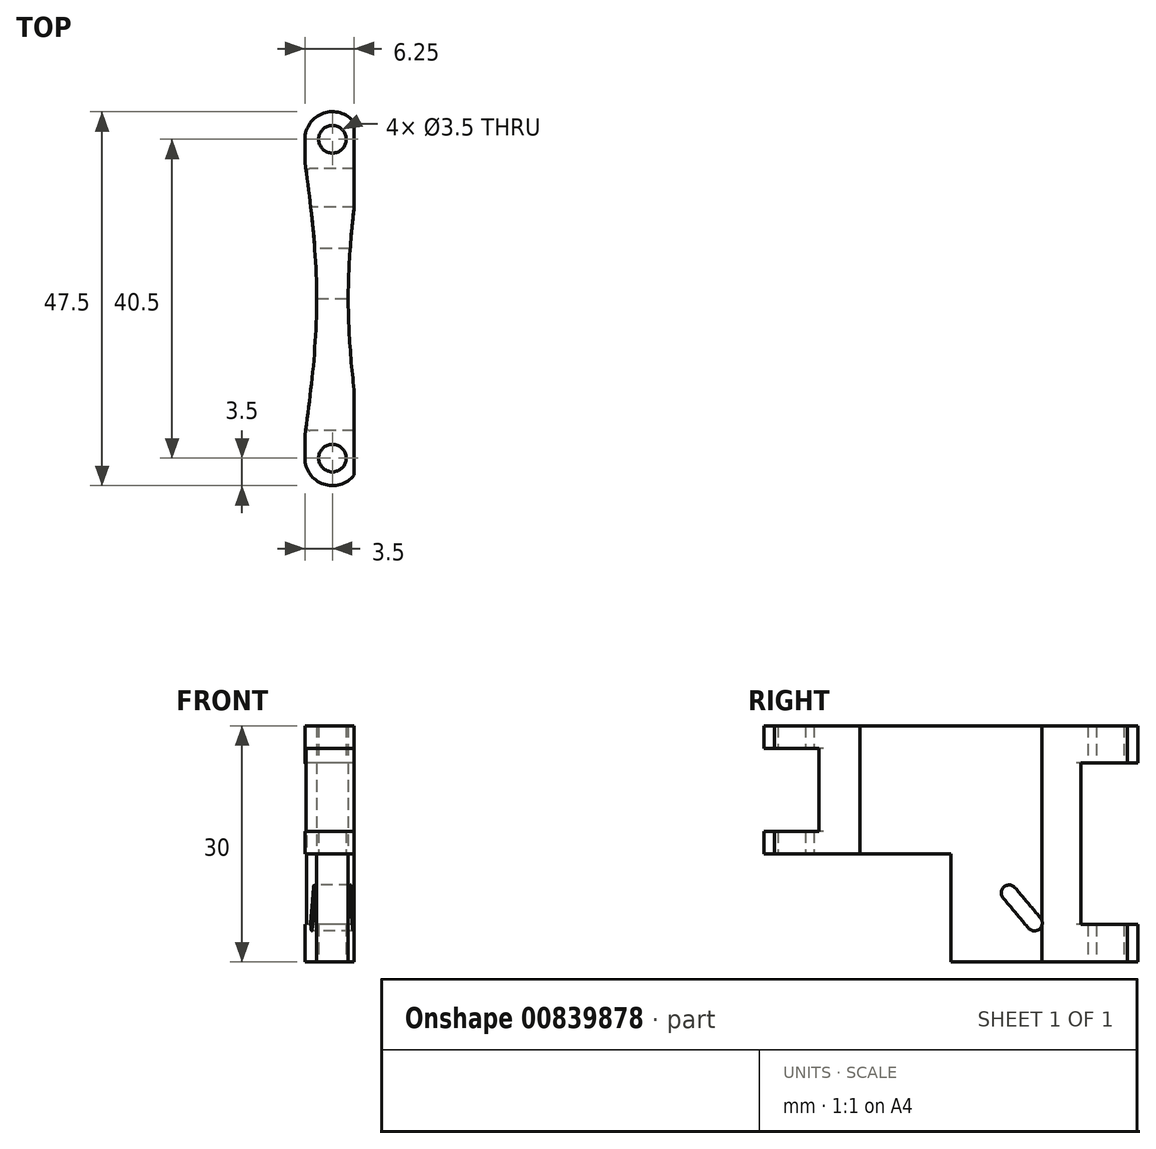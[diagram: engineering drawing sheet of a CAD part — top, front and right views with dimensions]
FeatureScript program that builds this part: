
annotation { "Feature Type Name" : "Feature", "Feature Type Description" : "" }
export const myFeature = defineFeature(function(context is Context, id is Id, definition is map)
    precondition{}
    {
        {
            var Q0;
            Q0=qCreatedBy(makeId("Top.planeOp"),FACE);
            var sketch = newSketch(context, id + "F0", { "sketchPlane" : qUnion([Q0])});
            skCircle(sketch, "E0", {"center": v(0, 0) * mm, "radius": 1.75 * mm});
            skCircle(sketch, "E1", {"center": v(0, 0) * mm, "radius": 3.5 * mm});
            skCircle(sketch, "E2", {"center": v(0, 40.5) * mm, "radius": 3.5 * mm});
            skCircle(sketch, "E3", {"center": v(0, 40.5) * mm, "radius": 1.75 * mm});
            skLineSegment(sketch, "E4", {"start": v(-3.5, 40.5) * mm, "end": v(-3.5, 0) * mm});
            skLineSegment(sketch, "E5", {"start": v(3.5, 40.5) * mm, "end": v(3.5, 0) * mm});
            skLineSegment(sketch, "E6", {"start": v(-2, 37.63) * mm, "end": v(-2, 2.87) * mm, "construction": true});
            skLineSegment(sketch, "E7", {"start": v(-2, 20.25) * mm, "end": v(-3.5, 20.25) * mm, "construction": true});
            skFitSpline(sketch, "E8", {"points": [v(-3.5, 37.63) * mm, v(-2, 20.25) * mm, v(-3.5, 2.87) * mm], "startDerivative": vector(4.5, -32.27) * mm, "endDerivative": vector(-4.5, -32.27) * mm});
            skLineSegment(sketch, "E9", {"start": v(-2.75, 20.25) * mm, "end": v(-2.75, 38.33) * mm, "construction": true});
            skLineSegment(sketch, "E10", {"start": v(-2.75, 20.25) * mm, "end": v(-2.75, 2.17) * mm, "construction": true});
            skFitSpline(sketch, "E11.MirrorCS", {"points": [v(3.5, 37.63) * mm, v(2, 20.25) * mm, v(3.5, 2.87) * mm], "startDerivative": vector(-4.5, -32.27) * mm, "endDerivative": vector(4.5, -32.27) * mm});
            skLineSegment(sketch, "E12", {"start": v(-3.5, 20.25) * mm, "end": v(3.5, 20.25) * mm});
            skSolve(sketch);
        }
        {
            var Q0;
            {var subQ0=sQuery(id+"F0.wireOp",EDGE,"E8");var subQ1=sQuery(id+"F0.wireOp",EDGE,"E2");var subQ2=makeQuery(id+"F0.imprint","INTERSECT",VERTEX,{"disambiguationData":[OD(1.0)],"derivedFrom":[subQ1,subQ0]});Q0=makeQuery(id+"F0.imprint","IMPRINT",FACE,{"disambiguationData":[TD([[makeQuery(id+"F0.imprint","IMPRINT",EDGE,{"disambiguationData":[TD([[subQ2,-1.0]])],"derivedFrom":subQ1}),-1.0]])]});}
            var Q1;
            {var subQ0=sQuery(id+"F0.wireOp",EDGE,"E11.MirrorCS");var subQ1=sQuery(id+"F0.wireOp",EDGE,"E1");var subQ2=makeQuery(id+"F0.imprint","INTERSECT",VERTEX,{"disambiguationData":[OD(1.0)],"derivedFrom":[subQ1,subQ0]});Q1=makeQuery(id+"F0.imprint","IMPRINT",FACE,{"disambiguationData":[TD([[makeQuery(id+"F0.imprint","IMPRINT",EDGE,{"disambiguationData":[TD([[subQ2,-1.0]])],"derivedFrom":subQ1}),-1.0]])]});}
            var Q2;
            Q2=makeQuery(id+"F0.imprint","IMPRINT",FACE,{"disambiguationData":[TD([[makeQuery(id+"F0.imprint","IMPRINT",EDGE,{"derivedFrom":sQuery(id+"F0.wireOp",EDGE,"E0")}),-1.0]])]});
            var Q3;
            Q3=makeQuery(id+"F0.imprint","IMPRINT",FACE,{"disambiguationData":[TD([[makeQuery(id+"F0.imprint","IMPRINT",EDGE,{"derivedFrom":sQuery(id+"F0.wireOp",EDGE,"E3")}),-1.0]])]});
            var Q4;
            {var subQ1=sQuery(id+"F0.wireOp",EDGE,"E2");var subQ5=sQuery(id+"F0.wireOp",EDGE,"E4");var subQ6=makeQuery(id+"F0.imprint","INTERSECT",VERTEX,{"derivedFrom":[subQ1,subQ5]});Q4=makeQuery(id+"F0.imprint","IMPRINT",FACE,{"disambiguationData":[TD([[makeQuery(id+"F0.imprint","IMPRINT",EDGE,{"disambiguationData":[TD([[subQ6,-1.0]])],"derivedFrom":subQ1}),-1.0]])]});}
            var Q5;
            {var subQ1=sQuery(id+"F0.wireOp",EDGE,"E4");var subQ6=sQuery(id+"F0.wireOp",EDGE,"E1");var subQ10=makeQuery(id+"F0.imprint","INTERSECT",VERTEX,{"derivedFrom":[subQ6,subQ1]});Q5=makeQuery(id+"F0.imprint","IMPRINT",FACE,{"disambiguationData":[TD([[makeQuery(id+"F0.imprint","IMPRINT",EDGE,{"disambiguationData":[TD([[subQ10,1.0]])],"derivedFrom":subQ6}),-1.0]])]});}
            extrude(context, id + "F1", {"entities" : qUnion([Q0, Q1, Q2, Q3, Q4, Q5]), "depth" : (30 - 13.7) * mm, "offsetDistance" : 25 * mm});
        }
        {
            var Q0;
            {var subQ0=sQuery(id+"F0.wireOp",EDGE,"E4");Q0=makeQuery(id+"F1.opExtrude","SWEPT_FACE",FACE,{"disambiguationData":[OSD([subQ0]),TDD([makeQuery(id+"F0.imprint","IMPRINT",EDGE,{"disambiguationData":[TD([[makeQuery(id+"F0.imprint","INTERSECT",VERTEX,{"derivedFrom":[sQuery(id+"F0.wireOp",EDGE,"E1"),subQ0]}),1.0]])],"derivedFrom":subQ0})])]});}
            var sketch = newSketch(context, id + "F2", { "sketchPlane" : qUnion([Q0])});
            skLineSegment(sketch, "E13.bottom", {"start": v(3.5, 2.9) * mm, "end": v(-3.5, 2.9) * mm});
            skLineSegment(sketch, "E13.top", {"start": v(3.5, 13.4) * mm, "end": v(-3.5, 13.4) * mm});
            skLineSegment(sketch, "E13.left", {"start": v(3.5, 2.9) * mm, "end": v(3.5, 13.4) * mm});
            skLineSegment(sketch, "E13.right", {"start": v(-3.5, 2.9) * mm, "end": v(-3.5, 13.4) * mm});
            skPoint(sketch, "E13.middle", {"position": v(0, 8.15) * mm});
            skSolve(sketch);
        }
        {
            var Q0;
            {var subQ0=sQuery(id+"F2.wireOp",EDGE,"E13.right");Q0=makeQuery(id+"F2.imprint","IMPRINT",FACE,{"disambiguationData":[TD([[makeQuery(id+"F2.imprint","IMPRINT",EDGE,{"derivedFrom":subQ0}),-1.0]])]});}
            var Q1;
            {var subQ0=sQuery(id+"F2.wireOp",EDGE,"E13.bottom");var subQ1=sQuery(id+"F0.wireOp",EDGE,"E4");var subQ2=makeQuery(id+"F1.opExtrude","SWEPT_EDGE",EDGE,{"disambiguationData":[OSD([sQuery(id+"F0.wireOp",EDGE,"E1"),subQ1])]});var subQ3=makeQuery(id+"F2.imprint","INTERSECT",VERTEX,{"derivedFrom":[subQ2,subQ0]});Q1=makeQuery(id+"F2.imprint","IMPRINT",FACE,{"disambiguationData":[TD([[makeQuery(id+"F2.imprint","IMPRINT",EDGE,{"disambiguationData":[TD([[subQ3,-1.0]])],"derivedFrom":subQ0}),-1.0]])]});}
            var Q2;
            {var subQ0=sQuery(id+"F2.wireOp",EDGE,"E13.left");Q2=makeQuery(id+"F2.imprint","IMPRINT",FACE,{"disambiguationData":[TD([[makeQuery(id+"F2.imprint","IMPRINT",EDGE,{"derivedFrom":subQ0}),1.0]])]});}
            extrude(context, id + "F3", {"entities" : qUnion([Q0, Q1, Q2]), "operationType" : NewBodyOperationType.REMOVE, "oppositeDirection" : true, "depth" : 25 * mm, "offsetDistance" : 25 * mm});
        }
        {
            var Q0;
            Q0=makeQuery(id+"F0.imprint","IMPRINT",FACE,{"disambiguationData":[TD([[makeQuery(id+"F0.imprint","IMPRINT",EDGE,{"derivedFrom":sQuery(id+"F0.wireOp",EDGE,"E3")}),-1.0]])]});
            var Q1;
            {var subQ1=sQuery(id+"F0.wireOp",EDGE,"E2");var subQ5=sQuery(id+"F0.wireOp",EDGE,"E4");var subQ6=makeQuery(id+"F0.imprint","INTERSECT",VERTEX,{"derivedFrom":[subQ1,subQ5]});Q1=makeQuery(id+"F0.imprint","IMPRINT",FACE,{"disambiguationData":[TD([[makeQuery(id+"F0.imprint","IMPRINT",EDGE,{"disambiguationData":[TD([[subQ6,-1.0]])],"derivedFrom":subQ1}),-1.0]])]});}
            extrude(context, id + "F4", {"entities" : qUnion([Q0, Q1]), "operationType" : NewBodyOperationType.ADD, "depth" : -13.7 * mm, "offsetDistance" : 25 * mm});
        }
        {
            var Q0;
            {var subQ0=sQuery(id+"F0.wireOp",EDGE,"E4");Q0=makeQuery(id+"F4.boolean.opBoolean","MERGE",FACE,{"derivedFrom":[makeQuery(id+"F1.opExtrude","SWEPT_FACE",FACE,{"disambiguationData":[OSD([subQ0]),TDD([makeQuery(id+"F0.imprint","IMPRINT",EDGE,{"disambiguationData":[TD([[makeQuery(id+"F0.imprint","INTERSECT",VERTEX,{"derivedFrom":[sQuery(id+"F0.wireOp",EDGE,"E2"),subQ0]}),-1.0]])],"derivedFrom":subQ0})])]}),makeQuery(id+"F4.opExtrude","SWEPT_FACE",FACE,{"disambiguationData":[OSD([subQ0])]})]});}
            var sketch = newSketch(context, id + "F5", { "sketchPlane" : qUnion([Q0])});
            skLineSegment(sketch, "E14.bottom", {"start": v(-36.75, 11.55) * mm, "end": v(-44.25, 11.55) * mm});
            skLineSegment(sketch, "E14.top", {"start": v(-36.75, -8.95) * mm, "end": v(-44.25, -8.95) * mm});
            skLineSegment(sketch, "E14.left", {"start": v(-36.75, 11.55) * mm, "end": v(-36.75, -8.95) * mm});
            skLineSegment(sketch, "E14.right", {"start": v(-44.25, 11.55) * mm, "end": v(-44.25, -8.95) * mm});
            skPoint(sketch, "E14.middle", {"position": v(-40.5, 1.3) * mm});
            skLineSegment(sketch, "E15", {"start": v(-21.75, 0) * mm, "end": v(-36.75, 0) * mm, "construction": true});
            skLineSegment(sketch, "E16", {"start": v(-36.75, 0) * mm, "end": v(-36.75, -13.7) * mm, "construction": true});
            skLineSegment(sketch, "E17", {"start": v(-36.75, -13.7) * mm, "end": v(-21.75, -13.7) * mm, "construction": true});
            skLineSegment(sketch, "E18", {"start": v(-21.75, -13.7) * mm, "end": v(-21.75, 0) * mm, "construction": true});
            skLineSegment(sketch, "E19", {"start": v(-21.75, 0) * mm, "end": v(-21.75, -6.85) * mm, "construction": true});
            skLineSegment(sketch, "E20", {"start": v(-21.75, -13.7) * mm, "end": v(-21.75, -6.85) * mm, "construction": true});
            skCircle(sketch, "E21", {"center": v(-30.86, -8.77) * mm, "radius": 1 * mm});
            skCircle(sketch, "E22", {"center": v(-27.64, -4.93) * mm, "radius": 1 * mm});
            skLineSegment(sketch, "E23", {"start": v(-28.4, -4.3) * mm, "end": v(-31.62, -8.12) * mm});
            skLineSegment(sketch, "E24", {"start": v(-26.88, -5.58) * mm, "end": v(-30.1, -9.4) * mm});
            skLineSegment(sketch, "E25", {"start": v(-21.75, -6.85) * mm, "end": v(-36.75, -6.85) * mm, "construction": true});
            skLineSegment(sketch, "E26", {"start": v(-29.25, -6.85) * mm, "end": v(-27.64, -4.93) * mm, "construction": true});
            skLineSegment(sketch, "E27", {"start": v(-29.25, -6.85) * mm, "end": v(-30.86, -8.77) * mm, "construction": true});
            skLineSegment(sketch, "E28", {"start": v(-29.25, -6.85) * mm, "end": v(-21.75, -6.85) * mm, "construction": true});
            skSolve(sketch);
        }
        {
            var Q0;
            {var subQ0=sQuery(id+"F5.wireOp",EDGE,"E14.right");Q0=makeQuery(id+"F5.imprint","IMPRINT",FACE,{"disambiguationData":[TD([[makeQuery(id+"F5.imprint","IMPRINT",EDGE,{"derivedFrom":subQ0}),1.0]])]});}
            var Q1;
            {var subQ0=sQuery(id+"F5.wireOp",EDGE,"E14.bottom");var subQ2=sQuery(id+"F0.wireOp",EDGE,"E4");var subQ5=sQuery(id+"F0.wireOp",EDGE,"E2");var subQ6=makeQuery(id+"F4.boolean.opBoolean","MERGE",EDGE,{"derivedFrom":[makeQuery(id+"F1.opExtrude","SWEPT_EDGE",EDGE,{"disambiguationData":[OSD([subQ5,subQ2])]}),makeQuery(id+"F4.opExtrude","SWEPT_EDGE",EDGE,{"disambiguationData":[OSD([subQ5,subQ2])]})]});var subQ7=makeQuery(id+"F5.imprint","INTERSECT",VERTEX,{"derivedFrom":[subQ6,subQ0]});Q1=makeQuery(id+"F5.imprint","IMPRINT",FACE,{"disambiguationData":[TD([[makeQuery(id+"F5.imprint","IMPRINT",EDGE,{"disambiguationData":[TD([[subQ7,1.0]])],"derivedFrom":subQ0}),1.0]])]});}
            var Q2;
            {var subQ0=sQuery(id+"F5.wireOp",EDGE,"E14.left");Q2=makeQuery(id+"F5.imprint","IMPRINT",FACE,{"disambiguationData":[TD([[makeQuery(id+"F5.imprint","IMPRINT",EDGE,{"derivedFrom":subQ0}),-1.0]])]});}
            var Q3;
            {var subQ0=sQuery(id+"F5.wireOp",EDGE,"E21");var subQ1=makeQuery(id+"F5.imprint","INTERSECT",VERTEX,{"derivedFrom":[subQ0,sQuery(id+"F5.wireOp",EDGE,"E23")]});Q3=makeQuery(id+"F5.imprint","IMPRINT",FACE,{"disambiguationData":[TD([[makeQuery(id+"F5.imprint","IMPRINT",EDGE,{"disambiguationData":[TD([[subQ1,-1.0]])],"derivedFrom":subQ0}),1.0]])]});}
            var Q4;
            {var subQ0=sQuery(id+"F5.wireOp",EDGE,"E23");Q4=makeQuery(id+"F5.imprint","IMPRINT",FACE,{"disambiguationData":[TD([[makeQuery(id+"F5.imprint","IMPRINT",EDGE,{"derivedFrom":subQ0}),1.0]])]});}
            var Q5;
            {var subQ0=sQuery(id+"F5.wireOp",EDGE,"E22");var subQ1=makeQuery(id+"F5.imprint","INTERSECT",VERTEX,{"derivedFrom":[subQ0,sQuery(id+"F5.wireOp",EDGE,"E23")]});Q5=makeQuery(id+"F5.imprint","IMPRINT",FACE,{"disambiguationData":[TD([[makeQuery(id+"F5.imprint","IMPRINT",EDGE,{"disambiguationData":[TD([[subQ1,-1.0]])],"derivedFrom":subQ0}),1.0]])]});}
            extrude(context, id + "F6", {"entities" : qUnion([Q0, Q1, Q2, Q3, Q4, Q5]), "operationType" : NewBodyOperationType.REMOVE, "oppositeDirection" : true, "depth" : 25 * mm, "offsetDistance" : 25 * mm});
        }
        {
            var Q0;
            Q0=makeQuery(id+"F3.boolean.opBoolean","INTERSECT",EDGE,{"derivedFrom":[makeQuery(id+"F1.opExtrude","SWEPT_FACE",FACE,{"disambiguationData":[OSD([sQuery(id+"F0.wireOp",EDGE,"E8")])]}),makeQuery(id+"F3.opExtrude","SWEPT_FACE",FACE,{"disambiguationData":[OSD([sQuery(id+"F2.wireOp",EDGE,"E13.right")])]})]});
            var Q1;
            Q1=makeQuery(id+"F3.boolean.opBoolean","INTERSECT",EDGE,{"derivedFrom":[makeQuery(id+"F1.opExtrude","SWEPT_FACE",FACE,{"disambiguationData":[OSD([sQuery(id+"F0.wireOp",EDGE,"E11.MirrorCS")])]}),makeQuery(id+"F3.opExtrude","SWEPT_FACE",FACE,{"disambiguationData":[OSD([sQuery(id+"F2.wireOp",EDGE,"E13.right")])]})]});
            var Q2;
            {var subQ0=sQuery(id+"F0.wireOp",EDGE,"E11.MirrorCS");Q2=makeQuery(id+"F6.boolean.opBoolean","INTERSECT",EDGE,{"derivedFrom":[makeQuery(id+"F4.boolean.opBoolean","MERGE",FACE,{"derivedFrom":[makeQuery(id+"F1.opExtrude","SWEPT_FACE",FACE,{"disambiguationData":[OSD([subQ0])]}),makeQuery(id+"F4.opExtrude","SWEPT_FACE",FACE,{"disambiguationData":[OSD([subQ0])]})]}),makeQuery(id+"F6.opExtrude","SWEPT_FACE",FACE,{"disambiguationData":[OSD([sQuery(id+"F5.wireOp",EDGE,"E14.left")])]})]});}
            var Q3;
            {var subQ0=sQuery(id+"F0.wireOp",EDGE,"E8");Q3=makeQuery(id+"F6.boolean.opBoolean","INTERSECT",EDGE,{"derivedFrom":[makeQuery(id+"F4.boolean.opBoolean","MERGE",FACE,{"derivedFrom":[makeQuery(id+"F1.opExtrude","SWEPT_FACE",FACE,{"disambiguationData":[OSD([subQ0])]}),makeQuery(id+"F4.opExtrude","SWEPT_FACE",FACE,{"disambiguationData":[OSD([subQ0])]})]}),makeQuery(id+"F6.opExtrude","SWEPT_FACE",FACE,{"disambiguationData":[OSD([sQuery(id+"F5.wireOp",EDGE,"E14.left")])]})]});}
            fillet(context, id + "F7", {"entities" : qUnion([Q0, Q1, Q2, Q3]), "radius" : .5 * mm, "tangentPropagation" : true, "allowEdgeOverflow" : false});
        }
        {
            var Q0;
            Q0=makeQuery(id+"F1.opExtrude","CAP_FACE",FACE,{"disambiguationData":[OSD([sQuery(id+"F0.wireOp",EDGE,"E0"),sQuery(id+"F0.wireOp",EDGE,"E1"),sQuery(id+"F0.wireOp",EDGE,"E2"),sQuery(id+"F0.wireOp",EDGE,"E3"),sQuery(id+"F0.wireOp",EDGE,"E4"),sQuery(id+"F0.wireOp",EDGE,"E5"),sQuery(id+"F0.wireOp",EDGE,"E8"),sQuery(id+"F0.wireOp",EDGE,"E11.MirrorCS")])],"isStart":false});
            var sketch = newSketch(context, id + "F8", { "sketchPlane" : qUnion([Q0])});
            skLineSegment(sketch, "E29", {"start": v(2.75, 44) * mm, "end": v(2.75, -3.5) * mm});
            skPoint(sketch, "E29.endSnap0", {"position": v(0, -3.5) * mm});
            skLineSegment(sketch, "E30", {"start": v(0, -3.5) * mm, "end": v(0, 44) * mm, "construction": true});
            skLineSegment(sketch, "E31", {"start": v(0, 44) * mm, "end": v(5.67, 44) * mm, "construction": true});
            skSolve(sketch);
        }
        {
            var Q0;
            {var subQ1=sQuery(id+"F0.wireOp",EDGE,"E2");var subQ7=sQuery(id+"F0.wireOp",EDGE,"E5");var subQ8=makeQuery(id+"F1.opExtrude","CAP_EDGE",EDGE,{"disambiguationData":[OSD([subQ7]),TDD([makeQuery(id+"F0.imprint","IMPRINT",EDGE,{"disambiguationData":[TD([[makeQuery(id+"F0.imprint","INTERSECT",VERTEX,{"derivedFrom":[subQ1,subQ7]}),-1.0]])],"derivedFrom":subQ7})])],"isStart":false});Q0=makeQuery(id+"F8.imprint","IMPRINT",FACE,{"disambiguationData":[TD([[makeQuery(id+"F8.imprint","IMPRINT",EDGE,{"derivedFrom":subQ8}),-1.0]])]});}
            var Q1;
            {var subQ1=sQuery(id+"F0.wireOp",EDGE,"E1");var subQ7=sQuery(id+"F0.wireOp",EDGE,"E5");var subQ8=makeQuery(id+"F1.opExtrude","CAP_EDGE",EDGE,{"disambiguationData":[OSD([subQ7]),TDD([makeQuery(id+"F0.imprint","IMPRINT",EDGE,{"disambiguationData":[TD([[makeQuery(id+"F0.imprint","INTERSECT",VERTEX,{"derivedFrom":[subQ1,subQ7]}),1.0]])],"derivedFrom":subQ7})])],"isStart":false});Q1=makeQuery(id+"F8.imprint","IMPRINT",FACE,{"disambiguationData":[TD([[makeQuery(id+"F8.imprint","IMPRINT",EDGE,{"derivedFrom":subQ8}),-1.0]])]});}
            extrude(context, id + "F9", {"entities" : qUnion([Q0, Q1]), "operationType" : NewBodyOperationType.REMOVE, "oppositeDirection" : true, "depth" : 44 * mm, "offsetDistance" : 25 * mm});
        }
    });
